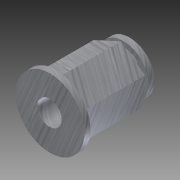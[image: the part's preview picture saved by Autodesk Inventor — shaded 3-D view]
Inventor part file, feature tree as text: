
AUTODESK INVENTOR PART (.ipt)
format: ipt  version: 2012 (Build 160160000, 160)  size: 139,264 bytes
history: native  units: in
note: dims shown in document units (in); Inventor stores cm internally (conversion verified against a paired STEP export)
features: extrude x5, sketch x5, reference x3, plane x1, projected_geometry x1
ambient origin geometry x8: Origin, YZ Plane, XZ Plane, XY Plane, X Axis, Y Axis, Z Axis, Center Point
bodies: Solid1 (feature_tree)
feature tree (15):
  extrude  "Extrusion1"  Depth=0.0591in TaperAngle=0.0deg
  extrude  "Extrusion2"  Depth=0.2362in
  plane  "Work Plane1"
  sketch  "Sketch3"  dims[d9=0.0591in d10=0.0in d13=0.0591in d14=0.0in]
  extrude  "Extrusion4"  Depth=0.0591in TaperAngle=0.0deg
  extrude  "Extrusion6"  Depth=0.3897in
  extrude  "Extrusion7"  [1 undecoded]
  sketch  "Sketch1"  dims[d0=0.0394in d1=0.0591in d2=0.0in]
  reference  "Reference1"
  sketch  "Sketch2"  dims[d3=0.7181in d4=0.0in d8=0.2362in]
  reference  "Reference2"
  reference  "Reference3"
  projected_geometry  "Projected Loop1"
  sketch  "Sketch4"  dims[d15=0.0591in d16=0.0in d17=0.3897in]
  sketch  "Sketch6"
note: 1 required parameter value undecoded (feature->parameter linkage not recoverable at this tier; creation-order binding heuristic only, values carry confidence <= 0.55)
